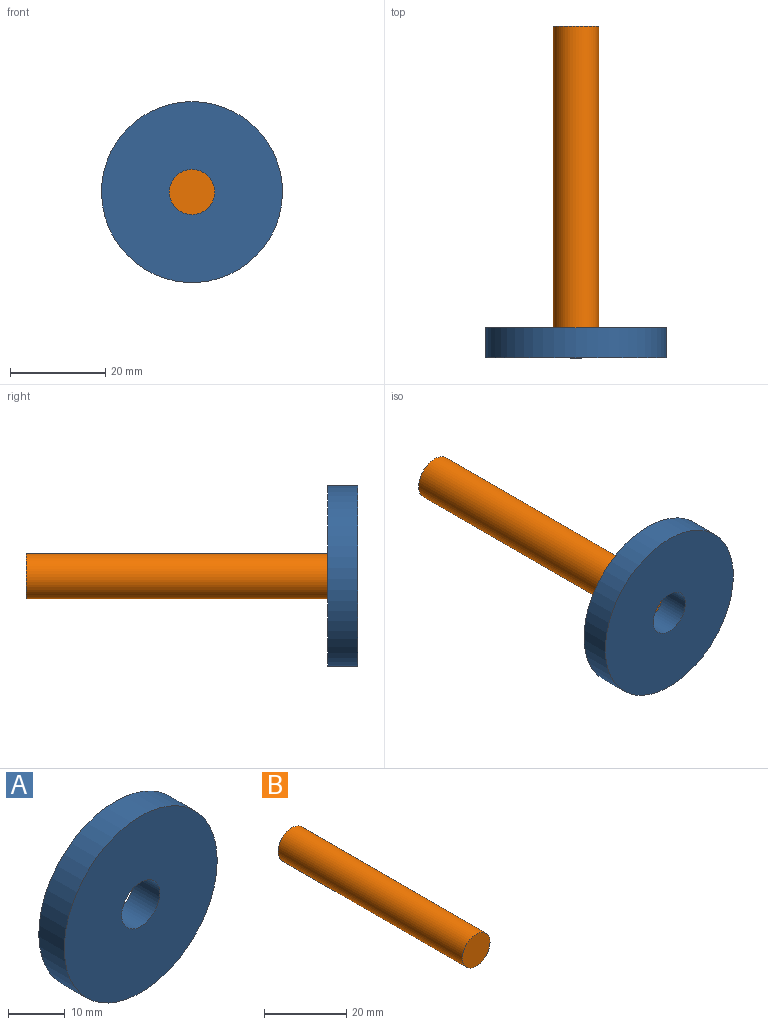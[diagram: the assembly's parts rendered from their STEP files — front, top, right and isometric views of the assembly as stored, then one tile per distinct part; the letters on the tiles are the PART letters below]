
ASSEMBLY  parts=2 mates=1
PART A: 4 faces, bbox 38.1x6.4x38.1 mm
  f0: cylinder r=4.76mm len=9.53mm, axis (0,-1,0), area 190mm2, adj f2,f3
  f1: cylinder r=19.05mm len=38.1mm, axis (0,-1,0), area 760.1mm2, adj f2,f3
  f2: plane 38.1x38.1mm, normal (0,1,0), area 1068.8mm2, adj f0,f1
  f3: plane 38.1x38.1mm, normal (0,-1,0), area 1068.8mm2, adj f0,f1
PART B: 3 faces, bbox 9.5x63.5x9.5 mm
  f0: plane 9.53x9.53mm, normal (0,1,0), area 71.3mm2, adj f1
  f1: cylinder r=4.76mm len=63.5mm, axis (0,-1,0), area 1900.2mm2, adj f0,f2
  f2: plane 9.53x9.53mm, normal (0,-1,0), area 71.3mm2, adj f1
PLACE A t=(-31.75,-66.67,0)mm
PLACE B t=(-31.75,-60.32,0)mm
MATE fastened A.f1 <-> B.f1  axis (0,1,0) through (0,6.35,0)mm
